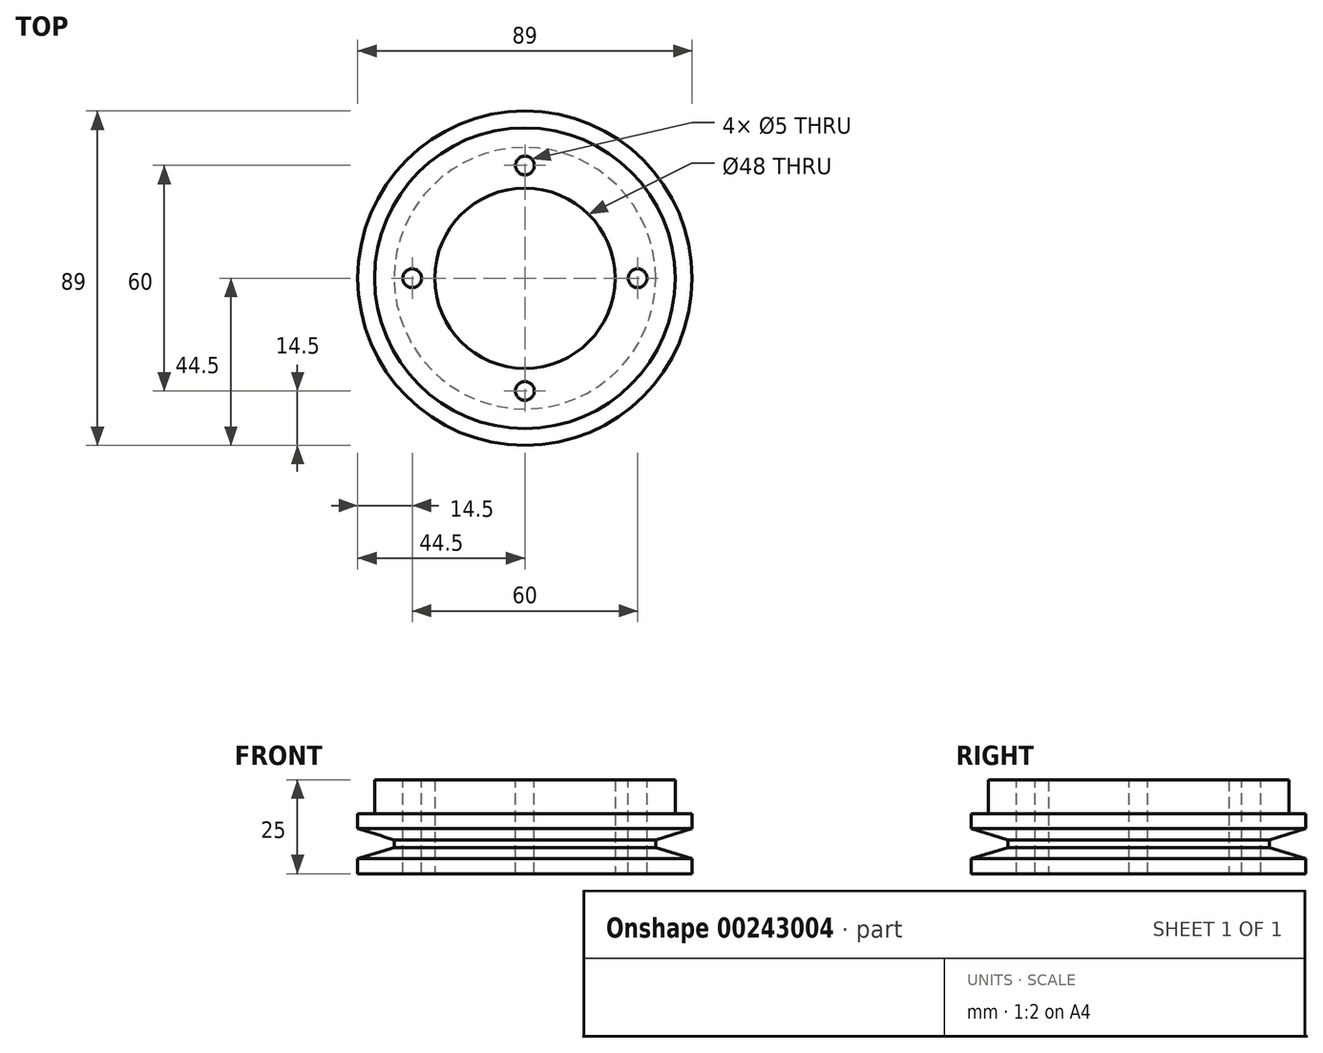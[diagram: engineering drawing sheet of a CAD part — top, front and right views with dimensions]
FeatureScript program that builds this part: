
annotation { "Feature Type Name" : "Feature", "Feature Type Description" : "" }
export const myFeature = defineFeature(function(context is Context, id is Id, definition is map)
    precondition{}
    {
        {
            var Q0;
            Q0=qCreatedBy(makeId("Top.planeOp"),FACE);
            var sketch = newSketch(context, id + "F0", { "sketchPlane" : qUnion([Q0])});
            skCircle(sketch, "E0", {"center": v(0, 0) * mm, "radius": 44.5 * mm});
            skCircle(sketch, "E1", {"center": v(0, 0) * mm, "radius": 40 * mm});
            skCircle(sketch, "E2", {"center": v(0, 0) * mm, "radius": 24 * mm});
            skSolve(sketch);
        }
        {
            var Q0;
            Q0=makeQuery(id+"F0.imprint","IMPRINT",FACE,{"disambiguationData":[TD([[makeQuery(id+"F0.imprint","IMPRINT",EDGE,{"derivedFrom":sQuery(id+"F0.wireOp",EDGE,"E0")}),1.0]])]});
            var Q1;
            Q1=makeQuery(id+"F0.imprint","IMPRINT",FACE,{"disambiguationData":[TD([[makeQuery(id+"F0.imprint","IMPRINT",EDGE,{"derivedFrom":sQuery(id+"F0.wireOp",EDGE,"E1")}),-1.0]])]});
            var Q2;
            Q2=makeQuery(id+"F0.imprint","IMPRINT",FACE,{"disambiguationData":[TD([[makeQuery(id+"F0.imprint","IMPRINT",EDGE,{"derivedFrom":sQuery(id+"F0.wireOp",EDGE,"E1")}),1.0]])]});
            extrude(context, id + "F1", {"entities" : qUnion([Q0, Q1, Q2]), "depth" : 16 * mm});
        }
        {
            var Q0;
            Q0=makeQuery(id+"F0.imprint","IMPRINT",FACE,{"disambiguationData":[TD([[makeQuery(id+"F0.imprint","IMPRINT",EDGE,{"derivedFrom":sQuery(id+"F0.wireOp",EDGE,"E1")}),1.0]])]});
            extrude(context, id + "F2", {"entities" : qUnion([Q0]), "operationType" : NewBodyOperationType.ADD, "depth" : 25 * mm});
        }
        {
            var Q0;
            Q0=qCreatedBy(makeId("Front.planeOp"),FACE);
            var sketch = newSketch(context, id + "F3", { "sketchPlane" : qUnion([Q0])});
            skLineSegment(sketch, "E3", {"start": v(-44.5, 12) * mm, "end": v(-34.8, 9.03) * mm});
            skLineSegment(sketch, "E4", {"start": v(-34.8, 6.97) * mm, "end": v(-44.5, 4) * mm});
            skLineSegment(sketch, "E5", {"start": v(-44.5, 4) * mm, "end": v(-44.5, 12) * mm});
            skLineSegment(sketch, "E6", {"start": v(-34.8, 9.03) * mm, "end": v(-34.8, 6.97) * mm});
            skPoint(sketch, "E7", {"position": v(-44.5, 8) * mm});
            skLineSegment(sketch, "E8", {"start": v(0, 0) * mm, "end": v(0, -11.25) * mm});
            skSolve(sketch);
        }
        {
            var Q0;
            Q0=qSketchRegion(id+"F3",true);
            var Q1;
            Q1=sQuery(id+"F3.wireOp",EDGE,"E8");
            revolve(context, id + "F4", {"operationType" : NewBodyOperationType.REMOVE, "entities" : qUnion([Q0]), "axis" : qUnion([Q1]), "revolveType" : RevolveType.FULL, "oppositeDirection" : true});
        }
        {
            var Q0;
            Q0=makeQuery(id+"F2.opExtrude","CAP_FACE",FACE,{"disambiguationData":[OSD([sQuery(id+"F0.wireOp",EDGE,"E1"),sQuery(id+"F0.wireOp",EDGE,"E2")])],"isStart":false});
            var sketch = newSketch(context, id + "F5", { "sketchPlane" : qUnion([Q0])});
            skCircle(sketch, "E9", {"center": v(0, 30) * mm, "radius": 2.5 * mm});
            skCircle(sketch, "E10", {"center": v(0, 0) * mm, "radius": 30 * mm, "construction": true});
            skCircle(sketch, "E11", {"center": v(30, 0) * mm, "radius": 2.5 * mm});
            skCircle(sketch, "E12", {"center": v(0, -30) * mm, "radius": 2.5 * mm});
            skCircle(sketch, "E13", {"center": v(-30, 0) * mm, "radius": 2.5 * mm});
            skSolve(sketch);
        }
        {
            var Q0;
            Q0 = qSketchRegion(id + "F5", true);
            var Q1;
            Q1 = qConstructionFilter(qBodyType(qCreatedBy(id + "F5" ,EDGE), BodyType.WIRE), ConstructionObject.NO);
            extrude(context, id + "F6", {"entities" : qUnion([Q0]), "operationType" : NewBodyOperationType.REMOVE, "surfaceEntities" : qUnion([Q1]), "oppositeDirection" : true, "depth" : 25 * mm});
        }
    });
